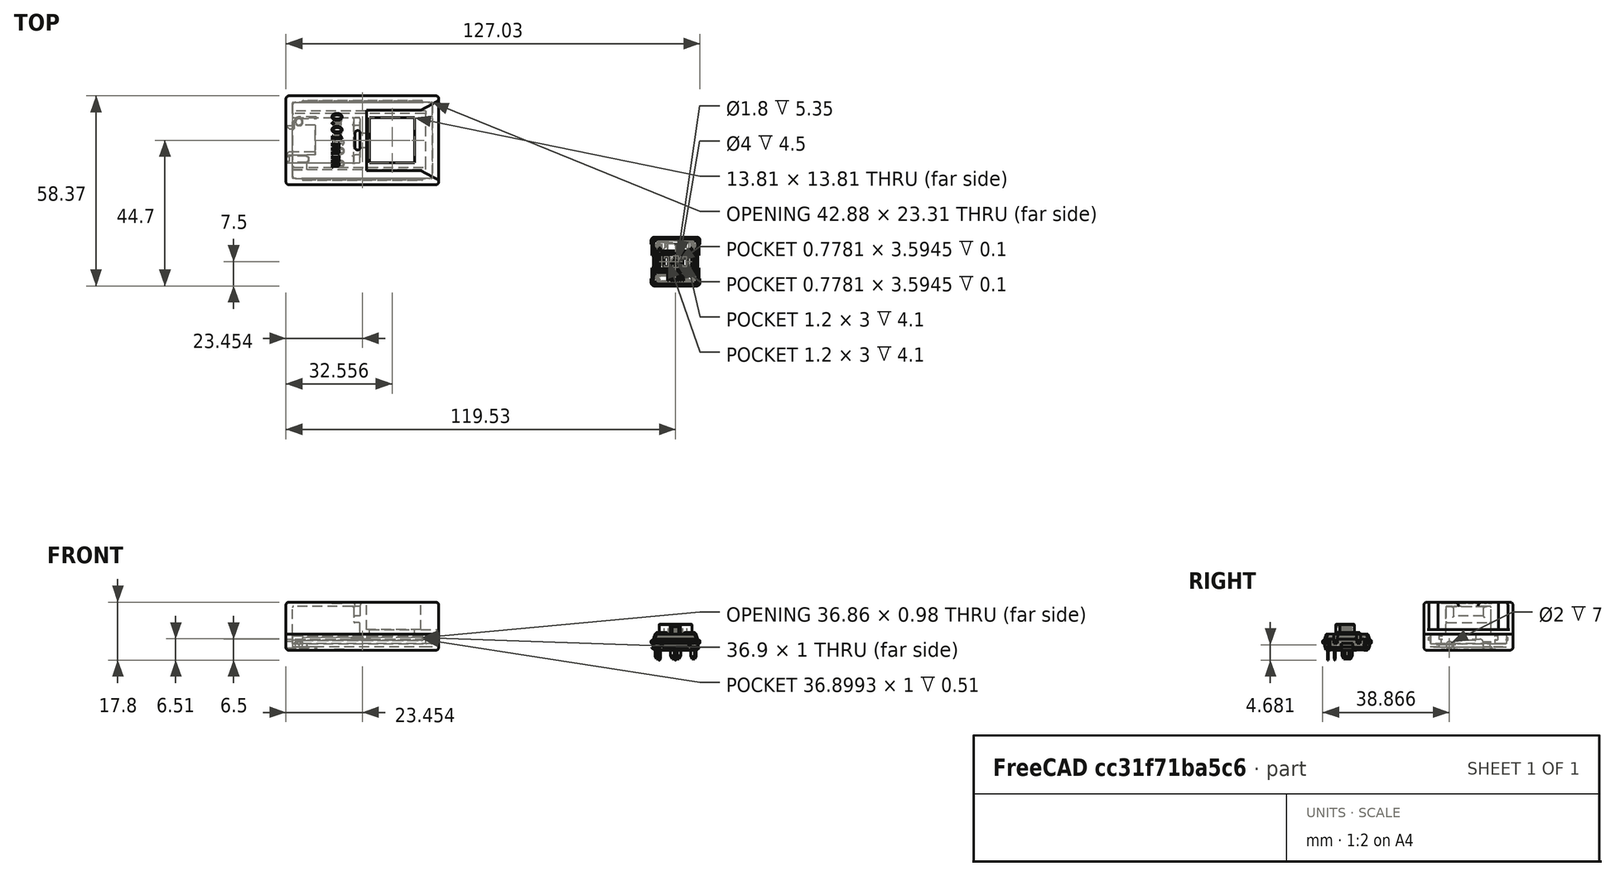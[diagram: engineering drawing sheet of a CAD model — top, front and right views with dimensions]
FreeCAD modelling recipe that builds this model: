
FCSTD DOCUMENT  (FreeCAD 1.1R42788 (Git))
Label: xiao_fit
License: All rights reserved
LicenseURL: https://en.wikipedia.org/wiki/All_rights_reserved
objects: Sketcher::SketchObject×21, PartDesign::Pocket×14, PartDesign::Pad×10, PartDesign::Fillet×10, Part::Feature×8, Mesh::Feature×6, App::Point×3, Part::Part2DObjectPython×2, PartDesign::Body×2, App::VarSet×1, PartDesign::SubShapeBinder×1, App::Part×1
note: 157 computed .brp shape members not serialized (recipe doc carries the construction recipe); baked Part::Feature solids carry a one-line shape summary decoded from their .brp

FEATURE [Mesh::Feature] SeeedXiao_01  label="SeeedXiao-01"
  Placement = pos=(-118.95,46.13,4.49) rot=(1,0,0;3.14159rad)
FEATURE [Sketcher::SketchObject] Sketch
  ArcFitTolerance = 1e-06
  AttachmentSupport = -> [XY_Plane]
  ExternalTypes = [0]
  FullyConstrained = false
  MakeInternals = false
  MapMode = 5
  sketch-geometry (4):
    g0: LineSegment StartX=-119.526 StartY=50.8652 StartZ=0 EndX=-119.526 EndY=23.5343 EndZ=0
    g1: LineSegment StartX=-119.526 StartY=23.5343 StartZ=0 EndX=-72.6263 EndY=23.5343 EndZ=0
    g2: LineSegment StartX=-72.6263 StartY=23.5343 StartZ=0 EndX=-72.6263 EndY=50.8652 EndZ=0
    g3: LineSegment StartX=-72.6263 StartY=50.8652 StartZ=0 EndX=-119.526 EndY=50.8652 EndZ=0
  constraints (8):
    c: Coincident(g0,g1)
    c: Coincident(g1,g2)
    c: Coincident(g2,g3)
    c: Coincident(g3,g0)
    c: Vertical(g0)
    c: Vertical(g2)
    c: Horizontal(g1)
    c: Horizontal(g3)
FEATURE [PartDesign::Pad] Pad
  Direction = (0,0,1)
  Length = 5
  Length2 = 10
  Profile = -> Sketch
  ReferenceAxis = -> Sketch [N_Axis]
  Refine = true
  Suppressed = false
  Type = 0
  expr: Length = VarSet.BottomHeight
FEATURE [Sketcher::SketchObject] Sketch001
  ArcFitTolerance = 1e-06
  AttachmentSupport = -> [Pad]
  ExternalGeometry = -> [Pad]
  ExternalTypes = [0]
  FullyConstrained = true
  MakeInternals = false
  MapMode = 5
  Placement = pos=(0,0,5) rot=(0,0,1;0rad)
  sketch-geometry (4):
    g0: LineSegment StartX=-117.526 StartY=48.8652 StartZ=0 EndX=-117.526 EndY=25.5343 EndZ=0
    g1: LineSegment StartX=-117.526 StartY=25.5343 StartZ=0 EndX=-74.6263 EndY=25.5343 EndZ=0
    g2: LineSegment StartX=-74.6263 StartY=25.5343 StartZ=0 EndX=-74.6263 EndY=48.8652 EndZ=0
    g3: LineSegment StartX=-74.6263 StartY=48.8652 StartZ=0 EndX=-117.526 EndY=48.8652 EndZ=0
  constraints (12):
    c: Coincident(g0,g1)
    c: Coincident(g1,g2)
    c: Coincident(g2,g3)
    c: Coincident(g3,g0)
    c: Vertical(g0)
    c: Vertical(g2)
    c: Horizontal(g1)
    c: Horizontal(g3)
    c: DistanceX(g-4,g0) = 2
    c: DistanceY(g0,g-4) = 2
    c: DistanceY(g-6,g1) = 2
    c: DistanceX(g1,g-6) = 2
FEATURE [PartDesign::Pocket] Pocket
  BaseFeature = -> Pad
  Direction = (0,0,-1)
  Length = 4
  Length2 = 5
  Profile = -> Sketch001
  ReferenceAxis = -> Sketch001 [N_Axis]
  Refine = true
  Suppressed = false
  Type = 0
  expr: Length = VarSet.BottomHeight - 1 mm
FEATURE [Sketcher::SketchObject] Sketch004
  ArcFitTolerance = 1e-06
  AttachmentSupport = -> [Pocket]
  ExternalGeometry = -> [Pocket]
  ExternalTypes = [0]
  FullyConstrained = true
  MakeInternals = false
  MapMode = 5
  Placement = pos=(0,0,1) rot=(0,0,1;0rad)
  sketch-geometry (4):
    g0: LineSegment StartX=-119.526 StartY=32.8652 StartZ=0 EndX=-119.526 EndY=28.1652 EndZ=0
    g1: LineSegment StartX=-119.526 StartY=28.1652 StartZ=0 EndX=-113.026 EndY=28.1652 EndZ=0
    g2: LineSegment StartX=-113.026 StartY=28.1652 StartZ=0 EndX=-113.026 EndY=32.8652 EndZ=0
    g3: LineSegment StartX=-113.026 StartY=32.8652 StartZ=0 EndX=-119.526 EndY=32.8652 EndZ=0
  constraints (12):
    c: Coincident(g0,g1)
    c: Coincident(g1,g2)
    c: Coincident(g2,g3)
    c: Coincident(g3,g0)
    c: Vertical(g0)
    c: Vertical(g2)
    c: Horizontal(g1)
    c: Horizontal(g3)
    c: PointOnObject(g0,g-3)
    c: DistanceY(g2,g-4) = 16
    c: DistanceX(g-5,g2) = 4.5
    c: DistanceY(g2,g2) = 4.7
FEATURE [PartDesign::Pad] Pad001  label="LED-Fiber"
  BaseFeature = -> Pocket
  Direction = (0,0,1)
  Length = 1
  Length2 = 10
  Profile = -> Sketch004
  ReferenceAxis = -> Sketch004 [N_Axis]
  Refine = true
  Suppressed = false
  Type = 0
FEATURE [Sketcher::SketchObject] Sketch005
  ArcFitTolerance = 1e-06
  AttachmentSupport = -> [Pad001]
  ExternalTypes = [0]
  FullyConstrained = false
  MakeInternals = false
  MapMode = 5
  Placement = pos=(-119.526,0,0) rot=(0.57735,-0.57735,-0.57735;2.0944rad)
  sketch-geometry (10):
    g0: LineSegment StartX=-41.7963 StartY=2.3456 StartZ=0 EndX=-41.7963 EndY=1.0544 EndZ=0
    g1: LineSegment StartX=-40.7419 StartY=0 StartZ=0 EndX=-33.7507 EndY=0 EndZ=0
    g2: LineSegment StartX=-32.6963 StartY=1.0544 StartZ=0 EndX=-32.6963 EndY=2.3456 EndZ=0
    g3: LineSegment StartX=-33.7507 StartY=3.4 StartZ=0 EndX=-40.7419 EndY=3.4 EndZ=0
    g4: ArcOfCircle CenterX=-40.7419 CenterY=2.3456 CenterZ=0 NormalX=0 NormalY=0 NormalZ=1 AngleXU=0 Radius=1.0544 StartAngle=1.5708 EndAngle=3.14159
    g5: ArcOfCircle CenterX=-40.7419 CenterY=1.0544 CenterZ=0 NormalX=0 NormalY=0 NormalZ=1 AngleXU=0 Radius=1.0544 StartAngle=3.14159 EndAngle=4.71239
    g6: ArcOfCircle CenterX=-33.7507 CenterY=1.0544 CenterZ=0 NormalX=0 NormalY=0 NormalZ=1 AngleXU=0 Radius=1.0544 StartAngle=4.71239 EndAngle=6.28319
    g7: ArcOfCircle CenterX=-33.7507 CenterY=2.3456 CenterZ=0 NormalX=0 NormalY=0 NormalZ=1 AngleXU=0 Radius=1.0544 StartAngle=0 EndAngle=1.5708
    g8: GeomPoint [constr] X=-41.7963 Y=3.4 Z=0
    g9: GeomPoint [constr] X=-32.6963 Y=0 Z=0
  constraints (22):
    c: Tangent(g0,g4) = -1.5708
    c: Tangent(g0,g5) = -1.5708
    c: Tangent(g1,g5) = -1.5708
    c: Tangent(g1,g6) = -1.5708
    c: Tangent(g2,g6) = -1.5708
    c: Tangent(g2,g7) = -1.5708
    c: Tangent(g3,g7) = -1.5708
    c: Tangent(g3,g4) = -1.5708
    c: Vertical(g0)
    c: Vertical(g2)
    c: Horizontal(g1)
    c: Horizontal(g3)
    c: Equal(g4,g5)
    c: Equal(g5,g6)
    c: Equal(g6,g7)
    c: PointOnObject(g8,g0)
    c: PointOnObject(g8,g3)
    c: PointOnObject(g9,g1)
    c: PointOnObject(g9,g2)
    c: PointOnObject(g1,g-1)
    c: DistanceX(g0,g2) = 9.1
    c: Distance(g3,g1) = 3.4
FEATURE [Sketcher::SketchObject] Sketch006
  ArcFitTolerance = 1e-06
  AttachmentSupport = -> [Pocket]
  ExternalGeometry = -> [Pocket]
  ExternalTypes = [0]
  FullyConstrained = true
  MakeInternals = false
  MapMode = 5
  Placement = pos=(0,0,1) rot=(0,0,1;0rad)
  sketch-geometry (9):
    g0: ArcOfCircle CenterX=-115.526 CenterY=42.8652 CenterZ=0 NormalX=0 NormalY=0 NormalZ=1 AngleXU=0 Radius=1 StartAngle=1.5708 EndAngle=4.71239
    g1: ArcOfCircle CenterX=-110.326 CenterY=44.1152 CenterZ=0 NormalX=0 NormalY=0 NormalZ=1 AngleXU=0 Radius=0.25 StartAngle=4.71237 EndAngle=7.854
    g2: LineSegment StartX=-115.526 StartY=43.8652 StartZ=0 EndX=-110.326 EndY=43.8652 EndZ=0
    g3: LineSegment StartX=-110.326 StartY=44.3652 StartZ=0 EndX=-115.526 EndY=44.3652 EndZ=0
    g4: ArcOfCircle CenterX=-115.526 CenterY=42.8652 CenterZ=0 NormalX=0 NormalY=0 NormalZ=1 AngleXU=0 Radius=1.5 StartAngle=1.5708 EndAngle=3.14159
    g5: LineSegment StartX=-117.026 StartY=42.8652 StartZ=0 EndX=-117.026 EndY=34.8652 EndZ=0
    g6: LineSegment StartX=-117.026 StartY=34.8652 StartZ=0 EndX=-110.526 EndY=34.8652 EndZ=0
    g7: LineSegment StartX=-110.526 StartY=34.8652 StartZ=0 EndX=-110.526 EndY=41.8652 EndZ=0
    g8: LineSegment StartX=-110.526 StartY=41.8652 StartZ=0 EndX=-115.526 EndY=41.8652 EndZ=0
  constraints (27):
    c: Vertical(g0,g0)
    c: Vertical(g1,g1)
    c: Coincident(g2,g0)
    c: Coincident(g2,g1)
    c: Horizontal(g2)
    c: Coincident(g3,g1)
    c: Horizontal(g3)
    c: Vertical(g5)
    c: Coincident(g6,g5)
    c: Horizontal(g6)
    c: Coincident(g7,g6)
    c: Vertical(g7)
    c: Coincident(g8,g7)
    c: Coincident(g8,g0)
    c: Horizontal(g8)
    c: Tangent(g5,g4) = -1.5708
    c: Coincident(g0,g4)
    c: DistanceX(g-5,g1) = 7.2
    c: Distance(g0,g-4) = 2
    c: DistanceX(g4,g0) = 1.5
    c: Tangent(g3,g4) = -1.5708
    c: DistanceY(g7,g1) = 2
    c: DistanceY(g0,g-5) = 6
    c: Radius(g0) = 1
    c: Radius(g1) = 0.25
    c: DistanceY(g7,g7) = 7
    c: DistanceX(g-3,g6) = 9
FEATURE [PartDesign::Pocket] Pocket002  label="ResetLever"
  BaseFeature = -> Pad001
  Direction = (0,0,-1)
  Length = 5
  Length2 = 5
  Profile = -> Sketch006
  ReferenceAxis = -> Sketch006 [N_Axis]
  Refine = true
  Suppressed = false
  Type = 1
FEATURE [Sketcher::SketchObject] Sketch007
  ArcFitTolerance = 1e-06
  AttachmentSupport = -> [Pocket002]
  ExternalGeometry = -> [Pocket002]
  ExternalTypes = [0]
  FullyConstrained = true
  MakeInternals = false
  MapMode = 5
  Placement = pos=(0,0,1) rot=(0,0,1;0rad)
  sketch-geometry (1):
    g0: Circle CenterX=-115.526 CenterY=42.8652 CenterZ=0 NormalX=0 NormalY=0 NormalZ=1 AngleXU=0 Radius=0.95
  constraints (2):
    c: Diameter(g0) = 1.9
    c: Coincident(g0,g-3)
FEATURE [PartDesign::Pad] Pad002  label="ResetBump"
  BaseFeature = -> Pocket002
  Direction = (0,0,1)
  Length = 1.6
  Length2 = 10
  Profile = -> Sketch007
  ReferenceAxis = -> Sketch007 [N_Axis]
  Refine = true
  Suppressed = false
  TaperAngle = 10
  Type = 0
FEATURE [PartDesign::Pocket] Pocket001  label="USB-Side"
  BaseFeature = -> Pad002
  Direction = (1,0,0)
  Length = 9
  Length2 = 5
  Profile = -> Sketch005
  ReferenceAxis = -> Sketch005 [N_Axis]
  Refine = true
  Suppressed = false
  Type = 0
FEATURE [Sketcher::SketchObject] Sketch008
  ArcFitTolerance = 1e-06
  AttachmentSupport = -> [Pocket001]
  ExternalTypes = [0]
  FullyConstrained = false
  MakeInternals = false
  MapMode = 5
  Placement = pos=(-119.526,0,0) rot=(0.57735,-0.57735,-0.57735;2.0944rad)
  sketch-geometry (1):
    g0: Circle CenterX=-31.3663 CenterY=1.68065 CenterZ=0 NormalX=0 NormalY=0 NormalZ=1 AngleXU=0 Radius=1
  constraints (1):
    c: Diameter(g0) = 2
FEATURE [PartDesign::Pocket] Pocket003  label="LED-Light"
  BaseFeature = -> Pocket001
  Direction = (1,0,0)
  Length = 7
  Length2 = 5
  Profile = -> Sketch008
  ReferenceAxis = -> Sketch008 [N_Axis]
  Refine = true
  Suppressed = false
  Type = 0
FEATURE [App::VarSet] VarSet
  BottomHeight = 5
  Tolerance = 0.01
  XiaoLength = 21
  XiaoWidth = 17.5
FEATURE [Part::Feature] Part__Feature  label="bottom_stabilizer"
  shape: bbox 15.16 x 15.16 x 5.85 mm, 308 faces (baked)
FEATURE [Part::Feature] Part__Feature001  label="contact"
  Placement = pos=(0,-5.9,0) rot=(0,0,1;0rad)
  shape: bbox 1.2 x 2.241 x 2.141 mm, 33 faces (baked)
FEATURE [Part::Feature] Part__Feature002  label="pin1"
  Placement = pos=(0,-5.9,0) rot=(0,0,1;0rad)
  shape: bbox 9.72 x 2.05 x 7 mm, 141 faces (baked)
FEATURE [Part::Feature] Part__Feature003  label="pin2"
  Placement = pos=(-5,-3.8,0) rot=(0,0,1;0rad)
  shape: bbox 3.2 x 0.65 x 7 mm, 30 faces (baked)
FEATURE [Part::Feature] Part__Feature004  label="top_stabilizer"
  Placement = pos=(0,0,3) rot=(0,0,1;0rad)
  shape: bbox 14.5 x 13.8 x 7.5 mm, 348 faces (baked)
FEATURE [Part::Feature] Part__Feature005  label="stabilizer"
  Placement = pos=(0,6.25,3) rot=(-1,0,0;0.20944rad)
  shape: bbox 9.432 x 7.756 x 2.155 mm, 7 faces (baked)
FEATURE [Part::Feature] Part__Feature006  label="stem_stabilizer"
  Placement = pos=(0,0,3.3) rot=(0,0,1;0rad)
  shape: bbox 11.5 x 5.7 x 7 mm, 99 faces (baked)
FEATURE [Part::Feature] Part__Feature007  label="shrunken_spring"
  Placement = pos=(0,0,4.15) rot=(0,0,1;0rad)
  shape: bbox 3.3 x 3.3 x 7.484 mm, 14 faces (baked)
FEATURE [PartDesign::SubShapeBinder] Binder
  BindCopyOnChange = 0
  BindMode = 0
  ClaimChildren = false
  Context = -> Body001 [Binder.]
  Fuse = false
  MakeFace = true
  OffsetFill = false
  OffsetIntersection = false
  OffsetJoinType = 0
  OffsetOpenResult = false
  PartialLoad = false
  Refine = true
  Relative = true
  Support = -> [Body[Pad.Face6]]
  _Version = 2
FEATURE [PartDesign::Pad] Pad004
  Direction = (0,0,1)
  Length = 1.3
  Length2 = 10
  Profile = -> Binder
  Refine = true
  Suppressed = false
  Type = 0
FEATURE [Sketcher::SketchObject] Sketch010
  ArcFitTolerance = 1e-06
  AttachmentSupport = -> [Pad004]
  ExternalGeometry = -> [Pad004]
  ExternalTypes = [0]
  FullyConstrained = true
  MakeInternals = false
  MapMode = 5
  Placement = pos=(0,0,5) rot=(1,0,0;3.14159rad)
  expr: Constraints[10] = 2 mm + VarSet.Tolerance
  expr: Constraints[16] = 2 mm + VarSet.Tolerance
  expr: Constraints[9] = 2 mm + VarSet.Tolerance
  sketch-geometry (7):
    g0: LineSegment StartX=-117.516 StartY=-25.5443 StartZ=0 EndX=-117.516 EndY=-48.8552 EndZ=0
    g1: LineSegment StartX=-117.516 StartY=-48.8552 StartZ=0 EndX=-74.6363 EndY=-48.8552 EndZ=0
    g2: LineSegment StartX=-74.6363 StartY=-48.8552 StartZ=0 EndX=-74.6363 EndY=-25.5443 EndZ=0
    g3: LineSegment StartX=-74.6363 StartY=-25.5443 StartZ=0 EndX=-117.516 EndY=-25.5443 EndZ=0
    g4: GeomPoint [constr] X=-96.0759 Y=-37.1997 Z=0
    g5: LineSegment [constr] StartX=-119.526 StartY=-50.8652 StartZ=0 EndX=-117.516 EndY=-48.8552 EndZ=0
    g6: LineSegment [constr] StartX=-119.526 StartY=-23.5343 StartZ=0 EndX=-117.516 EndY=-25.5443 EndZ=0
  constraints (17):
    c: Coincident(g0,g1)
    c: Coincident(g1,g2)
    c: Coincident(g2,g3)
    c: Coincident(g3,g0)
    c: Vertical(g0)
    c: Vertical(g2)
    c: Horizontal(g1)
    c: Horizontal(g3)
    c: Symmetric(g2,g0,g4)
    c: Distance(g0,g-4) = 2.01
    c: DistanceX(g1,g-6) = 2.01
    c: Coincident(g5,g-6)
    c: Coincident(g5,g0)
    c: Coincident(g6,g-4)
    c: Coincident(g6,g0)
    c: Equal(g6,g5)
    c: DistanceY(g0,g6) = 2.01
FEATURE [Sketcher::SketchObject] Sketch012
  ArcFitTolerance = 1e-06
  ExternalTypes = [0]
  FullyConstrained = true
  MakeInternals = false
  MapMode = 5
  Placement = pos=(0,48.8652,0) rot=(1,0,0;1.5708rad)
  sketch-geometry (6):
    g0: LineSegment [constr] StartX=-117.526 StartY=5 StartZ=0 EndX=-117.526 EndY=1 EndZ=0
    g1: LineSegment [constr] StartX=-74.6263 StartY=5 StartZ=0 EndX=-74.6263 EndY=1 EndZ=0
    g2: LineSegment StartX=-114.526 StartY=4 StartZ=0 EndX=-114.526 EndY=3 EndZ=0
    g3: LineSegment StartX=-114.526 StartY=3 StartZ=0 EndX=-77.6263 EndY=3 EndZ=0
    g4: LineSegment StartX=-77.6263 StartY=3 StartZ=0 EndX=-77.6263 EndY=4 EndZ=0
    g5: LineSegment StartX=-77.6263 StartY=4 StartZ=0 EndX=-114.526 EndY=4 EndZ=0
  constraints (16):
    c: Coincident(g0,g-3)
    c: Coincident(g0,g-3)
    c: Coincident(g1,g-4)
    c: Coincident(g1,g-4)
    c: Coincident(g2,g3)
    c: Coincident(g3,g4)
    c: Coincident(g4,g5)
    c: Coincident(g5,g2)
    c: Vertical(g2)
    c: Vertical(g4)
    c: Horizontal(g3)
    c: Horizontal(g5)
    c: DistanceY(g2,g0) = 2
    c: DistanceY(g2,g2) = 1
    c: DistanceX(g0,g2) = 3
    c: DistanceX(g4,g1) = 3
FEATURE [PartDesign::Pocket] Pocket005
  BaseFeature = -> Pocket003
  Direction = (0,1,-2e-16)
  Length = 0.51
  Length2 = 5
  Profile = -> Sketch012
  ReferenceAxis = -> Sketch012 [N_Axis]
  Refine = true
  Suppressed = false
  Type = 0
  expr: Length = 0.5 mm + VarSet.Tolerance
FEATURE [Sketcher::SketchObject] Sketch013
  ArcFitTolerance = 1e-06
  AttachmentSupport = -> [Pocket005]
  ExternalGeometry = -> [Pocket005]
  ExternalTypes = [0]
  FullyConstrained = true
  MakeInternals = false
  MapMode = 5
  Placement = pos=(0,25.5343,0) rot=(0,0.707107,0.707107;3.14159rad)
  sketch-geometry (4):
    g0: LineSegment StartX=77.6263 StartY=4 StartZ=0 EndX=77.6263 EndY=3 EndZ=0
    g1: LineSegment StartX=77.6263 StartY=3 StartZ=0 EndX=114.526 EndY=3 EndZ=0
    g2: LineSegment StartX=114.526 StartY=3 StartZ=0 EndX=114.526 EndY=4 EndZ=0
    g3: LineSegment StartX=114.526 StartY=4 StartZ=0 EndX=77.6263 EndY=4 EndZ=0
  constraints (12):
    c: Coincident(g0,g1)
    c: Coincident(g1,g2)
    c: Coincident(g2,g3)
    c: Coincident(g3,g0)
    c: Vertical(g0)
    c: Vertical(g2)
    c: Horizontal(g1)
    c: Horizontal(g3)
    c: DistanceX(g-3,g0) = 3
    c: DistanceX(g2,g-4) = 3
    c: DistanceY(g0,g-3) = 2
    c: Distance(g0,g0) = 1
FEATURE [PartDesign::Pocket] Pocket006
  BaseFeature = -> Pocket005
  Direction = (0,-1,2e-16)
  Length = 0.51
  Length2 = 5
  Profile = -> Sketch013
  ReferenceAxis = -> Sketch013 [N_Axis]
  Refine = true
  Suppressed = false
  Type = 0
  expr: Length = 0.5 mm + VarSet.Tolerance
FEATURE [Mesh::Feature] MBK_Keycap___1u  label="MBK_Keycap_-_1u"
  Placement = pos=(0,0,6.61) rot=(0,0,1;0rad)
FEATURE [App::Part] red  label="Choc"
  Group = -> [Part__Feature,Part__Feature001,Part__Feature002,Part__Feature003,Part__Feature004,Part__Feature005,Part__Feature006,Part__Feature007,MBK_Keycap___1u]
  Origin = -> Origin001
  Placement = pos=(-86.93,37.19,4.1) rot=(0,0,1;0rad)
  expr: .Placement.Base.z = VarSet.BottomHeight + 1.3 mm - 2.2 mm
FEATURE [PartDesign::Fillet] Fillet005
  Base = -> Pocket006 [Edge11,Edge5,Edge2,Edge1]
  BaseFeature = -> Pocket006
  Radius = 1
  Refine = true
  SupportTransform = false
  Suppressed = false
  UseAllEdges = false
FEATURE [PartDesign::Fillet] Fillet006
  Base = -> Fillet005 [Edge8]
  BaseFeature = -> Fillet005
  Radius = 1
  Refine = true
  SupportTransform = false
  Suppressed = false
  UseAllEdges = false
FEATURE [PartDesign::Fillet] Fillet007
  Base = -> Fillet006 [Edge83,Edge78,Edge63,Edge76]
  BaseFeature = -> Fillet006
  Radius = 1
  Refine = true
  SupportTransform = false
  Suppressed = false
  UseAllEdges = false
FEATURE [PartDesign::Fillet] Fillet009
  Base = -> Pad004 [Edge8,Edge1,Edge5,Edge2]
  BaseFeature = -> Pad004
  Radius = 1
  Refine = true
  SupportTransform = false
  Suppressed = false
  UseAllEdges = false
FEATURE [PartDesign::Pad] Pad005
  BaseFeature = -> Fillet009
  Direction = (0,0,-1)
  Length = 3
  Length2 = 10
  Profile = -> Sketch010
  ReferenceAxis = -> Sketch010 [N_Axis]
  Refine = true
  Suppressed = false
  Type = 0
FEATURE [Sketcher::SketchObject] Sketch011
  ArcFitTolerance = 1e-06
  AttachmentSupport = -> [Pad005,Fillet009]
  ExternalGeometry = -> [Pad005]
  ExternalTypes = [0]
  FullyConstrained = true
  MakeInternals = false
  MapMode = 5
  Placement = pos=(0,0,2) rot=(1,0,0;3.14159rad)
  expr: Constraints[10] = VarSet.XiaoWidth - 1 mm
  sketch-geometry (6):
    g0: LineSegment StartX=-117.516 StartY=-28.9497 StartZ=0 EndX=-76.6363 EndY=-28.9497 EndZ=0
    g1: LineSegment StartX=-76.6363 StartY=-28.9497 StartZ=0 EndX=-76.6363 EndY=-45.4497 EndZ=0
    g2: LineSegment StartX=-76.6363 StartY=-45.4497 StartZ=0 EndX=-117.516 EndY=-45.4497 EndZ=0
    g3: LineSegment StartX=-117.516 StartY=-45.4497 StartZ=0 EndX=-117.516 EndY=-28.9497 EndZ=0
    g4: LineSegment [constr] StartX=-117.516 StartY=-25.5443 StartZ=0 EndX=-117.516 EndY=-28.9497 EndZ=0
    g5: LineSegment [constr] StartX=-117.516 StartY=-48.8552 StartZ=0 EndX=-117.516 EndY=-45.4497 EndZ=0
  constraints (16):
    c: PointOnObject(g0,g-3)
    c: Horizontal(g0)
    c: Coincident(g0,g1)
    c: Vertical(g1)
    c: Coincident(g1,g2)
    c: PointOnObject(g2,g-3)
    c: Horizontal(g2)
    c: DistanceX(g0,g-4) = 2
    c: Coincident(g2,g3)
    c: Coincident(g3,g0)
    c: DistanceY(g3,g3) = 16.5
    c: Coincident(g4,g-3)
    c: Coincident(g4,g0)
    c: Coincident(g5,g-3)
    c: Coincident(g5,g2)
    c: Equal(g5,g4)
FEATURE [PartDesign::Pocket] Pocket004
  BaseFeature = -> Pad005
  Direction = (0,0,1)
  Length = 0
  Length2 = 5
  Profile = -> Sketch011
  ReferenceAxis = -> Sketch011 [N_Axis]
  Refine = true
  Suppressed = false
  Type = 3
  UpToFace = -> Pad005 [Face2]
FEATURE [Sketcher::SketchObject] Sketch014
  ArcFitTolerance = 1e-06
  AttachmentSupport = -> [Pocket004]
  ExternalGeometry = -> [Pocket004]
  ExternalTypes = [0]
  FullyConstrained = true
  MakeInternals = false
  MapMode = 5
  Placement = pos=(0,48.8552,0) rot=(0,0.707107,0.707107;3.14159rad)
  expr: Constraints[11] = 3 mm + VarSet.Tolerance
  expr: Constraints[12] = VarSet.Tolerance + 3 mm
  expr: Constraints[8] = 1 mm - VarSet.Tolerance * 2
  sketch-geometry (6):
    g0: LineSegment StartX=77.6463 StartY=4 StartZ=0 EndX=77.6463 EndY=3.02 EndZ=0
    g1: LineSegment StartX=77.6463 StartY=3.02 StartZ=0 EndX=114.506 EndY=3.02 EndZ=0
    g2: LineSegment StartX=114.506 StartY=3.02 StartZ=0 EndX=114.506 EndY=4 EndZ=0
    g3: LineSegment StartX=114.506 StartY=4 StartZ=0 EndX=77.6463 EndY=4 EndZ=0
    g4: LineSegment [constr] StartX=74.6363 StartY=2 StartZ=0 EndX=117.516 EndY=2 EndZ=0
    g5: LineSegment [constr] StartX=117.516 StartY=5 StartZ=0 EndX=74.6363 EndY=5 EndZ=0
  constraints (16):
    c: Coincident(g0,g1)
    c: Coincident(g1,g2)
    c: Coincident(g2,g3)
    c: Coincident(g3,g0)
    c: Vertical(g0)
    c: Vertical(g2)
    c: Horizontal(g1)
    c: Horizontal(g3)
    c: DistanceY(g0,g0) = 0.98
    c: Coincident(g4,g-3)
    c: Coincident(g4,g-4)
    c: DistanceX(g4,g0) = 3.01
    c: DistanceX(g1,g4) = 3.01
    c: Coincident(g5,g-4)
    c: Coincident(g5,g-3)
    c: DistanceY(g0,g5) = 1
FEATURE [PartDesign::Pad] Pad006
  BaseFeature = -> Pocket004
  Direction = (0,1,-2e-16)
  Length = 0.5
  Length2 = 10
  Profile = -> Sketch014
  ReferenceAxis = -> Sketch014 [N_Axis]
  Refine = true
  Suppressed = false
  Type = 0
FEATURE [Sketcher::SketchObject] Sketch015
  ArcFitTolerance = 1e-06
  AttachmentSupport = -> [Pad006]
  ExternalGeometry = -> [Pad006]
  ExternalTypes = [0]
  FullyConstrained = true
  MakeInternals = false
  MapMode = 5
  Placement = pos=(0,25.5443,0) rot=(1,0,0;1.5708rad)
  expr: Constraints[10] = 3 mm + VarSet.Tolerance
  expr: Constraints[11] = 3 mm + VarSet.Tolerance
  expr: Constraints[12] = 1 mm - VarSet.Tolerance * 2
  sketch-geometry (5):
    g0: LineSegment [constr] StartX=-117.516 StartY=2 StartZ=0 EndX=-74.6363 EndY=2 EndZ=0
    g1: LineSegment StartX=-114.506 StartY=4 StartZ=0 EndX=-114.506 EndY=3.02 EndZ=0
    g2: LineSegment StartX=-114.506 StartY=3.02 StartZ=0 EndX=-77.6463 EndY=3.02 EndZ=0
    g3: LineSegment StartX=-77.6463 StartY=3.02 StartZ=0 EndX=-77.6463 EndY=4 EndZ=0
    g4: LineSegment StartX=-77.6463 StartY=4 StartZ=0 EndX=-114.506 EndY=4 EndZ=0
  constraints (14):
    c: Coincident(g0,g-3)
    c: Coincident(g0,g-4)
    c: Coincident(g1,g2)
    c: Coincident(g2,g3)
    c: Coincident(g3,g4)
    c: Coincident(g4,g1)
    c: Vertical(g1)
    c: Vertical(g3)
    c: Horizontal(g2)
    c: Horizontal(g4)
    c: DistanceX(g0,g1) = 3.01
    c: DistanceX(g2,g0) = 3.01
    c: Distance(g1,g1) = 0.98
    c: DistanceY(g1,g-3) = 1
FEATURE [PartDesign::Pad] Pad007
  BaseFeature = -> Pad006
  Direction = (0,-1,2e-16)
  Length = 0.5
  Length2 = 10
  Profile = -> Sketch015
  ReferenceAxis = -> Sketch015 [N_Axis]
  Refine = true
  Suppressed = false
  Type = 0
FEATURE [PartDesign::Fillet] Fillet
  Base = -> Pad007 [Edge59,Edge63,Edge61,Edge64,Edge57,Edge60,Edge58,Edge62,Edge66,Edge72,Edge70,Edge71,Edge67,Edge69,Edge68,Edge65]
  BaseFeature = -> Pad007
  Radius = 0.4
  Refine = true
  SupportTransform = false
  Suppressed = false
  UseAllEdges = false
FEATURE [Sketcher::SketchObject] Sketch016
  ArcFitTolerance = 1e-06
  AttachmentSupport = -> [Fillet]
  ExternalGeometry = -> [Fillet]
  ExternalTypes = [0]
  FullyConstrained = false
  MakeInternals = false
  MapMode = 5
  Placement = pos=(0,0,5) rot=(1,0,0;3.14159rad)
  expr: Constraints[8] = 13.8 mm + VarSet.Tolerance
  expr: Constraints[9] = 13.8 mm + VarSet.Tolerance
  sketch-geometry (6):
    g0: LineSegment StartX=-93.8788 StartY=-30.2947 StartZ=0 EndX=-93.8788 EndY=-44.1047 EndZ=0
    g1: LineSegment StartX=-93.8788 StartY=-44.1047 StartZ=0 EndX=-80.0688 EndY=-44.1047 EndZ=0
    g2: LineSegment StartX=-80.0688 StartY=-44.1047 StartZ=0 EndX=-80.0688 EndY=-30.2947 EndZ=0
    g3: LineSegment StartX=-80.0688 StartY=-30.2947 StartZ=0 EndX=-93.8788 EndY=-30.2947 EndZ=0
    g4: LineSegment [constr] StartX=-76.6363 StartY=-28.9497 StartZ=0 EndX=-80.0688 EndY=-30.2947 EndZ=0
    g5: LineSegment [constr] StartX=-76.6363 StartY=-45.4497 StartZ=0 EndX=-80.0688 EndY=-44.1047 EndZ=0
  constraints (15):
    c: Coincident(g0,g1)
    c: Coincident(g1,g2)
    c: Coincident(g2,g3)
    c: Coincident(g3,g0)
    c: Vertical(g0)
    c: Vertical(g2)
    c: Horizontal(g1)
    c: Horizontal(g3)
    c: Distance(g0,g2) = 13.81
    c: Distance(g1,g3) = 13.81
    c: Coincident(g4,g-3)
    c: Coincident(g4,g2)
    c: Coincident(g5,g-3)
    c: Coincident(g5,g1)
    c: Equal(g5,g4)
FEATURE [PartDesign::Pocket] Pocket007
  BaseFeature = -> Fillet
  Direction = (0,0,1)
  Length = 5
  Length2 = 5
  Profile = -> Sketch016
  ReferenceAxis = -> Sketch016 [N_Axis]
  Refine = true
  Suppressed = false
  Type = 1
FEATURE [Sketcher::SketchObject] Sketch017
  ArcFitTolerance = 1e-06
  AttachmentSupport = -> [Pocket007]
  ExternalGeometry = -> [Pocket007]
  ExternalTypes = [0]
  FullyConstrained = true
  MakeInternals = false
  MapMode = 5
  Placement = pos=(0,45.4497,0) rot=(1,0,0;1.5708rad)
  expr: Constraints[11] = 1.25 mm + VarSet.Tolerance
  sketch-geometry (4):
    g0: LineSegment StartX=-76.6363 StartY=4.5 StartZ=0 EndX=-117.516 EndY=4.5 EndZ=0
    g1: LineSegment StartX=-117.516 StartY=4.5 StartZ=0 EndX=-117.516 EndY=3.24 EndZ=0
    g2: LineSegment StartX=-117.516 StartY=3.24 StartZ=0 EndX=-76.6363 EndY=3.24 EndZ=0
    g3: LineSegment StartX=-76.6363 StartY=3.24 StartZ=0 EndX=-76.6363 EndY=4.5 EndZ=0
  constraints (12):
    c: Coincident(g0,g1)
    c: Coincident(g1,g2)
    c: Coincident(g2,g3)
    c: Coincident(g3,g0)
    c: Horizontal(g0)
    c: Horizontal(g2)
    c: Vertical(g1)
    c: Vertical(g3)
    c: PointOnObject(g0,g-4)
    c: PointOnObject(g1,g-3)
    c: DistanceY(g0,g-4) = 0.5
    c: DistanceY(g3,g3) = 1.26
FEATURE [PartDesign::Pocket] Pocket008
  BaseFeature = -> Pocket007
  Direction = (0,1,-2e-16)
  Length = 0.7
  Length2 = 5
  Profile = -> Sketch017
  ReferenceAxis = -> Sketch017 [N_Axis]
  Refine = true
  Suppressed = false
  Type = 0
FEATURE [Sketcher::SketchObject] Sketch018
  ArcFitTolerance = 1e-06
  AttachmentSupport = -> [Pocket008]
  ExternalGeometry = -> [Pocket008]
  ExternalTypes = [0]
  FullyConstrained = true
  MakeInternals = false
  MapMode = 5
  Placement = pos=(0,28.9497,0) rot=(0,0.707107,0.707107;3.14159rad)
  sketch-geometry (4):
    g0: LineSegment StartX=76.6363 StartY=4.5 StartZ=0 EndX=76.6363 EndY=3.25 EndZ=0
    g1: LineSegment StartX=76.6363 StartY=3.25 StartZ=0 EndX=117.516 EndY=3.25 EndZ=0
    g2: LineSegment StartX=117.516 StartY=3.25 StartZ=0 EndX=117.516 EndY=4.5 EndZ=0
    g3: LineSegment StartX=117.516 StartY=4.5 StartZ=0 EndX=76.6363 EndY=4.5 EndZ=0
  constraints (12):
    c: Coincident(g0,g1)
    c: Coincident(g1,g2)
    c: Coincident(g2,g3)
    c: Coincident(g3,g0)
    c: Vertical(g0)
    c: Vertical(g2)
    c: Horizontal(g1)
    c: Horizontal(g3)
    c: PointOnObject(g0,g-4)
    c: PointOnObject(g1,g-3)
    c: DistanceY(g2,g-3) = 0.5
    c: DistanceY(g2,g2) = 1.25
FEATURE [PartDesign::Pocket] Pocket009
  BaseFeature = -> Pocket008
  Direction = (0,-1,2e-16)
  Length = 0.7
  Length2 = 5
  Profile = -> Sketch018
  ReferenceAxis = -> Sketch018 [N_Axis]
  Refine = true
  Suppressed = false
  Type = 0
FEATURE [Sketcher::SketchObject] Sketch019
  ArcFitTolerance = 1e-06
  AttachmentSupport = -> [Pocket009]
  ExternalGeometry = -> [Pocket009]
  ExternalTypes = [0]
  FullyConstrained = false
  MakeInternals = false
  MapMode = 5
  Placement = pos=(0,0,5) rot=(1,0,0;3.14159rad)
  expr: Constraints[8] = VarSet.XiaoLength + VarSet.Tolerance
  sketch-geometry (6):
    g0: LineSegment StartX=-94.7718 StartY=-34.8937 StartZ=0 EndX=-96.5056 EndY=-34.8937 EndZ=0
    g1: LineSegment StartX=-96.5056 StartY=-34.8937 StartZ=0 EndX=-96.5056 EndY=-39.5058 EndZ=0
    g2: LineSegment StartX=-96.5056 StartY=-39.5058 StartZ=0 EndX=-94.7718 EndY=-39.5058 EndZ=0
    g3: LineSegment StartX=-94.7718 StartY=-39.5058 StartZ=0 EndX=-94.7718 EndY=-34.8937 EndZ=0
    g4: LineSegment [constr] StartX=-117.516 StartY=-45.4497 StartZ=0 EndX=-96.5056 EndY=-39.5058 EndZ=0
    g5: LineSegment [constr] StartX=-96.5056 StartY=-34.8937 StartZ=0 EndX=-117.516 EndY=-28.9497 EndZ=0
  constraints (14):
    c: Coincident(g0,g1)
    c: Coincident(g1,g2)
    c: Coincident(g2,g3)
    c: Coincident(g3,g0)
    c: Horizontal(g0)
    c: Horizontal(g2)
    c: Vertical(g1)
    c: Vertical(g3)
    c: DistanceX(g-4,g0) = 21.01
    c: Coincident(g4,g-5)
    c: Coincident(g4,g1)
    c: Coincident(g5,g0)
    c: Coincident(g5,g-4)
    c: Equal(g5,g4)
FEATURE [PartDesign::Pad] Pad008
  BaseFeature = -> Pocket009
  Direction = (0,0,-1)
  Length = 2
  Length2 = 10
  Profile = -> Sketch019
  ReferenceAxis = -> Sketch019 [N_Axis]
  Refine = true
  Suppressed = false
  Type = 0
FEATURE [PartDesign::Fillet] Fillet001
  Base = -> Pad008 [Edge133,Edge137,Edge129,Edge123,Edge107,Edge109,Edge106,Edge111,Edge29,Edge9]
  BaseFeature = -> Pad008
  Radius = 0.3
  Refine = true
  SupportTransform = false
  Suppressed = false
  UseAllEdges = false
FEATURE [PartDesign::Fillet] Fillet002
  Base = -> Fillet001 [Edge54,Edge36,Edge87,Edge17,Edge145,Edge149,Edge123,Edge50,Edge46,Edge3,Edge51,Edge58,Edge60]
  BaseFeature = -> Fillet001
  Radius = 0.3
  Refine = true
  SupportTransform = false
  Suppressed = false
  UseAllEdges = false
FEATURE [Sketcher::SketchObject] Sketch020
  ArcFitTolerance = 1e-06
  AttachmentSupport = -> [Fillet002]
  ExternalGeometry = -> [Fillet002]
  ExternalTypes = [0]
  FullyConstrained = false
  MakeInternals = false
  MapMode = 5
  Placement = pos=(0,0,6.3) rot=(0,0,1;0rad)
  sketch-geometry (12):
    g0: LineSegment StartX=-94.7635 StartY=46.4765 StartZ=0 EndX=-94.7635 EndY=27.8947 EndZ=0
    g1: LineSegment StartX=-94.7635 StartY=27.8947 StartZ=0 EndX=-78.1458 EndY=27.8947 EndZ=0
    g2: LineSegment StartX=-78.1458 StartY=46.4765 StartZ=0 EndX=-94.7635 EndY=46.4765 EndZ=0
    g3: LineSegment StartX=-118.526 StartY=50.8652 StartZ=0 EndX=-73.6263 EndY=50.8652 EndZ=0
    g4: LineSegment StartX=-119.526 StartY=49.8652 StartZ=0 EndX=-119.526 EndY=24.5374 EndZ=0
    g5: LineSegment StartX=-118.526 StartY=23.5343 StartZ=0 EndX=-73.6263 EndY=23.5343 EndZ=0
    g6: ArcOfCircle CenterX=-73.6263 CenterY=24.5343 CenterZ=0 NormalX=0 NormalY=0 NormalZ=1 AngleXU=0 Radius=1 StartAngle=4.71239 EndAngle=6.83956
    g7: ArcOfCircle CenterX=-118.526 CenterY=24.5343 CenterZ=0 NormalX=0 NormalY=0 NormalZ=1 AngleXU=0 Radius=1 StartAngle=3.13844 EndAngle=4.71239
    g8: ArcOfCircle CenterX=-118.526 CenterY=49.8652 CenterZ=0 NormalX=0 NormalY=0 NormalZ=1 AngleXU=0 Radius=1 StartAngle=1.5708 EndAngle=3.14159
    g9: ArcOfCircle CenterX=-73.6263 CenterY=49.8652 CenterZ=0 NormalX=0 NormalY=0 NormalZ=1 AngleXU=0 Radius=1 StartAngle=5.71161 EndAngle=7.85398
    g10: LineSegment StartX=-78.1458 StartY=46.4765 StartZ=0 EndX=-72.7853 EndY=49.3242 EndZ=0
    g11: LineSegment StartX=-78.1458 StartY=27.8947 StartZ=0 EndX=-72.7772 EndY=25.0624 EndZ=0
  constraints (25):
    c: Coincident(g0,g1)
    c: Coincident(g2,g0)
    c: Vertical(g0)
    c: Horizontal(g1)
    c: Horizontal(g2)
    c: Equal(g2,g1)
    c: Coincident(g6,g-5)
    c: Coincident(g6,g5)
    c: Coincident(g7,g-6)
    c: Coincident(g7,g5)
    c: Coincident(g7,g4)
    c: Coincident(g8,g-3)
    c: Coincident(g8,g3)
    c: Coincident(g3,g-3)
    c: Tangent(g4,g8) = -1.5708
    c: Coincident(g3,g-4)
    c: Coincident(g9,g-4)
    c: Coincident(g9,g3)
    c: Coincident(g10,g2)
    c: Coincident(g10,g9)
    c: Coincident(g11,g1)
    c: Coincident(g11,g6)
    c: Equal(g10,g11)
    c: Coincident(g5,g-5)
    c: Coincident(g5,g-6)
FEATURE [PartDesign::Pad] Pad009
  BaseFeature = -> Fillet002
  Direction = (0,0,1)
  Length = 8.5
  Length2 = 10
  Profile = -> Sketch020
  ReferenceAxis = -> Sketch020 [N_Axis]
  Refine = true
  Suppressed = false
  Type = 0
FEATURE [Sketcher::SketchObject] Sketch021
  ArcFitTolerance = 1e-06
  AttachmentSupport = -> [Pad009]
  ExternalGeometry = -> [Pad009]
  ExternalTypes = [0]
  FullyConstrained = true
  MakeInternals = false
  MapMode = 5
  Placement = pos=(0,0,5) rot=(1,0,0;3.14159rad)
  sketch-geometry (6):
    g0: LineSegment StartX=-117.526 StartY=-30.2497 StartZ=0 EndX=-117.526 EndY=-44.1497 EndZ=0
    g1: LineSegment StartX=-117.526 StartY=-44.1497 StartZ=0 EndX=-96.7635 EndY=-44.1497 EndZ=0
    g2: LineSegment StartX=-96.7635 StartY=-44.1497 StartZ=0 EndX=-96.7635 EndY=-30.2497 EndZ=0
    g3: LineSegment StartX=-96.7635 StartY=-30.2497 StartZ=0 EndX=-117.526 EndY=-30.2497 EndZ=0
    g4: LineSegment [constr] StartX=-119.526 StartY=-23.5343 StartZ=0 EndX=-117.526 EndY=-30.2497 EndZ=0
    g5: LineSegment [constr] StartX=-117.526 StartY=-44.1497 StartZ=0 EndX=-119.526 EndY=-50.8652 EndZ=0
  constraints (16):
    c: Coincident(g0,g1)
    c: Coincident(g1,g2)
    c: Coincident(g2,g3)
    c: Coincident(g3,g0)
    c: Vertical(g0)
    c: Vertical(g2)
    c: Horizontal(g1)
    c: Horizontal(g3)
    c: Coincident(g4,g-3)
    c: Coincident(g4,g0)
    c: Coincident(g5,g0)
    c: Coincident(g5,g-4)
    c: Equal(g4,g5)
    c: DistanceX(g4,g0) = 2
    c: DistanceX(g2,g-6) = 2
    c: DistanceY(g0,g-7) = 1
FEATURE [PartDesign::Pocket] Pocket010
  BaseFeature = -> Pad009
  Direction = (0,0,1)
  Length = 8.5
  Length2 = 5
  Profile = -> Sketch021
  ReferenceAxis = -> Sketch021 [N_Axis]
  Refine = true
  Suppressed = false
  Type = 0
FEATURE [Sketcher::SketchObject] Sketch023
  ArcFitTolerance = 1e-06
  AttachmentSupport = -> [Pocket010]
  ExternalGeometry = -> [Pocket010]
  ExternalTypes = [0]
  FullyConstrained = true
  MakeInternals = false
  MapMode = 5
  Placement = pos=(-96.7635,0,0) rot=(0.57735,-0.57735,-0.57735;2.0944rad)
  expr: Constraints[16] = 9 mm + 2 * VarSet.Tolerance
  expr: Constraints[20] = 3 mm + VarSet.Tolerance
  sketch-geometry (8):
    g0: LineSegment StartX=-41.7097 StartY=13.5 StartZ=0 EndX=-41.7097 EndY=10.49 EndZ=0
    g1: LineSegment StartX=-41.7097 StartY=10.49 StartZ=0 EndX=-32.6897 EndY=10.49 EndZ=0
    g2: LineSegment StartX=-32.6897 StartY=10.49 StartZ=0 EndX=-32.6897 EndY=13.5 EndZ=0
    g3: LineSegment StartX=-32.6897 StartY=13.5 StartZ=0 EndX=-30.2497 EndY=13.5 EndZ=0
    g4: LineSegment StartX=-30.2497 StartY=13.5 StartZ=0 EndX=-30.2497 EndY=8.49 EndZ=0
    g5: LineSegment StartX=-30.2497 StartY=8.49 StartZ=0 EndX=-44.1497 EndY=8.49 EndZ=0
    g6: LineSegment StartX=-44.1497 StartY=8.49 StartZ=0 EndX=-44.1497 EndY=13.5 EndZ=0
    g7: LineSegment StartX=-44.1497 StartY=13.5 StartZ=0 EndX=-41.7097 EndY=13.5 EndZ=0
  constraints (22):
    c: PointOnObject(g0,g-5)
    c: Vertical(g0)
    c: Coincident(g0,g1)
    c: Horizontal(g1)
    c: Coincident(g1,g2)
    c: PointOnObject(g2,g-5)
    c: Vertical(g2)
    c: Coincident(g2,g3)
    c: Coincident(g3,g4)
    c: Vertical(g4)
    c: Coincident(g4,g5)
    c: Horizontal(g5)
    c: Coincident(g5,g6)
    c: Vertical(g6)
    c: Coincident(g6,g7)
    c: Coincident(g7,g0)
    c: DistanceX(g1,g1) = 9.02
    c: Equal(g7,g3)
    c: Coincident(g3,g-5)
    c: Coincident(g6,g-5)
    c: DistanceY(g0,g0) = 3.01
    c: DistanceY(g4,g1) = 2
FEATURE [PartDesign::Pad] Pad010
  BaseFeature = -> Pocket010
  Direction = (-1,0,0)
  Length = 2
  Length2 = 10
  Profile = -> Sketch023
  ReferenceAxis = -> Sketch023 [N_Axis]
  Refine = true
  Suppressed = false
  Type = 0
FEATURE [Sketcher::SketchObject] Sketch024
  ArcFitTolerance = 1e-06
  AttachmentSupport = -> [Pad010]
  ExternalGeometry = -> [Pad010]
  ExternalTypes = [0]
  FullyConstrained = true
  MakeInternals = false
  MapMode = 5
  Placement = pos=(0,0,13.5) rot=(1,0,0;3.14159rad)
  expr: Constraints[3] = 1.5 mm + 2 * VarSet.Tolerance
  sketch-geometry (6):
    g0: LineSegment StartX=-98.2835 StartY=-34.9497 StartZ=0 EndX=-98.2835 EndY=-39.4497 EndZ=0
    g1: LineSegment StartX=-96.7635 StartY=-39.4497 StartZ=0 EndX=-96.7635 EndY=-34.9497 EndZ=0
    g2: LineSegment [constr] StartX=-96.7635 StartY=-32.6897 StartZ=0 EndX=-96.7635 EndY=-34.9497 EndZ=0
    g3: LineSegment [constr] StartX=-96.7635 StartY=-39.4497 StartZ=0 EndX=-96.7635 EndY=-41.7097 EndZ=0
    g4: ArcOfCircle CenterX=-97.5235 CenterY=-34.9497 CenterZ=0 NormalX=0 NormalY=0 NormalZ=1 AngleXU=0 Radius=0.76 StartAngle=2.58e-14 EndAngle=3.14159
    g5: ArcOfCircle CenterX=-97.5235 CenterY=-39.4497 CenterZ=0 NormalX=0 NormalY=0 NormalZ=1 AngleXU=0 Radius=0.76 StartAngle=3.14159 EndAngle=6.28319
  constraints (14):
    c: Vertical(g0)
    c: Vertical(g1)
    c: PointOnObject(g1,g-4)
    c: Distance(g1,g0) = 1.52
    c: DistanceY(g0,g0) = 4.5
    c: Coincident(g2,g-5)
    c: Coincident(g3,g-6)
    c: Equal(g2,g3)
    c: Tangent(g4,g0) = -1.5708
    c: Tangent(g4,g1) = -1.5708
    c: Tangent(g5,g0) = -1.5708
    c: Coincident(g1,g3)
    c: Tangent(g5,g1) = -1.5708
    c: Coincident(g1,g2)
FEATURE [PartDesign::Pocket] Pocket011
  BaseFeature = -> Pad010
  Direction = (0,0,1)
  Length = 5
  Length2 = 5
  Profile = -> Sketch024
  ReferenceAxis = -> Sketch024 [N_Axis]
  Refine = true
  Suppressed = false
  Type = 1
FEATURE [PartDesign::Fillet] Fillet008
  Base = -> Pocket011 [Edge212]
  BaseFeature = -> Pocket011
  Radius = 1.2
  Refine = true
  SupportTransform = false
  Suppressed = false
  UseAllEdges = false
FEATURE [PartDesign::Fillet] Fillet010
  Base = -> Fillet008 [Edge9]
  BaseFeature = -> Fillet008
  Radius = 1
  Refine = true
  SupportTransform = false
  Suppressed = false
  UseAllEdges = false
FEATURE [PartDesign::Fillet] Fillet011
  Base = -> Fillet010 [Edge139,Edge138,Edge136,Edge133,Edge130,Edge223,Edge198,Edge205,Edge129,Edge204,Edge199,Edge197,Edge201,Edge202,Edge134,Edge200,Edge128,Edge203]
  BaseFeature = -> Fillet010
  Radius = 0.4
  Refine = true
  SupportTransform = false
  Suppressed = false
  UseAllEdges = false
FEATURE [Part::Part2DObjectPython] ShapeString  # Draft 2D object (typed FeaturePython)
  FontFile = <path>
  Fuse = false
  Justification = 6
  JustificationReference = 0
  KeepLeftMargin = false
  MakeFace = true
  ObliqueAngle = 0
  Placement = pos=(-105.34,45.43,14.8) rot=(0,0,1;4.71239rad)
  ScaleToSize = true
  Size = 3
  String = 0.01mm
  Tracking = 0
FEATURE [PartDesign::Pocket] Pocket012
  BaseFeature = -> Fillet011
  Direction = (0,0,-1)
  Length = 0.3
  Length2 = 5
  Profile = -> ShapeString
  ReferenceAxis = -> ShapeString [N_Axis]
  Refine = true
  Suppressed = false
  Type = 0
FEATURE [PartDesign::Body] Body001  label="BodyLid"
  AllowCompound = false
  Group = -> [Binder,Pad004,Fillet009,Sketch010,Pad005,Sketch011,Pocket004,Sketch014,Pad006,Sketch015,Pad007,Fillet,Sketch016,Pocket007,Sketch017,Pocket008,Sketch018,Pocket009,Sketch019,Pad008,Fillet001,Fillet002,Sketch020,Pad009,Sketch021,Pocket010,Sketch023,Pad010,Sketch024,Pocket011,Fillet008,Fillet010,Fillet011,ShapeString,Pocket012]
  Origin = -> Origin002
  Tip = -> Pocket012
FEATURE [Part::Part2DObjectPython] ShapeString001  # Draft 2D object (typed FeaturePython)
  FontFile = <path>
  Fuse = false
  Justification = 6
  JustificationReference = 0
  KeepLeftMargin = false
  MakeFace = true
  ObliqueAngle = 0
  Placement = pos=(-104.64,28.97,0) rot=(0.707107,0.707107,0;3.14159rad)
  ScaleToSize = true
  Size = 3
  String = 0.01mm
  Tracking = 0
FEATURE [PartDesign::Pocket] Pocket013
  BaseFeature = -> Fillet007
  Direction = (-1e-16,1e-16,1)
  Length = 0.3
  Length2 = 5
  Profile = -> ShapeString001
  ReferenceAxis = -> ShapeString001 [N_Axis]
  Refine = true
  Suppressed = false
  Type = 0
FEATURE [PartDesign::Body] Body  label="BodyCase"
  AllowCompound = false
  Group = -> [Sketch,Pad,Sketch001,Pocket,Sketch004,Pad001,Sketch005,Sketch006,Pocket002,Sketch007,Pad002,Pocket001,Sketch008,Pocket003,Sketch012,Pocket005,Sketch013,Pocket006,Fillet005,Fillet006,Fillet007,ShapeString001,Pocket013]
  Origin = -> Origin
  Tip = -> Pocket013
FEATURE [Mesh::Feature] Mesh  label="BodyCase (0.02)"
FEATURE [Mesh::Feature] Mesh001  label="BodyLid (0.02)"
FEATURE [Mesh::Feature] Mesh002  label="BodyCase (0.01)"
FEATURE [Mesh::Feature] Mesh003  label="BodyLid (0.01)"
FEATURE [App::Point] Origin003  label="Origin"
  Role = Origin
FEATURE [App::Point] Origin004  label="Origin"
  Role = Origin
FEATURE [App::Point] Origin005  label="Origin"
  Role = Origin
note: 2 file-system paths scrubbed to <path> (originals preserved in the JSON sidecar)
